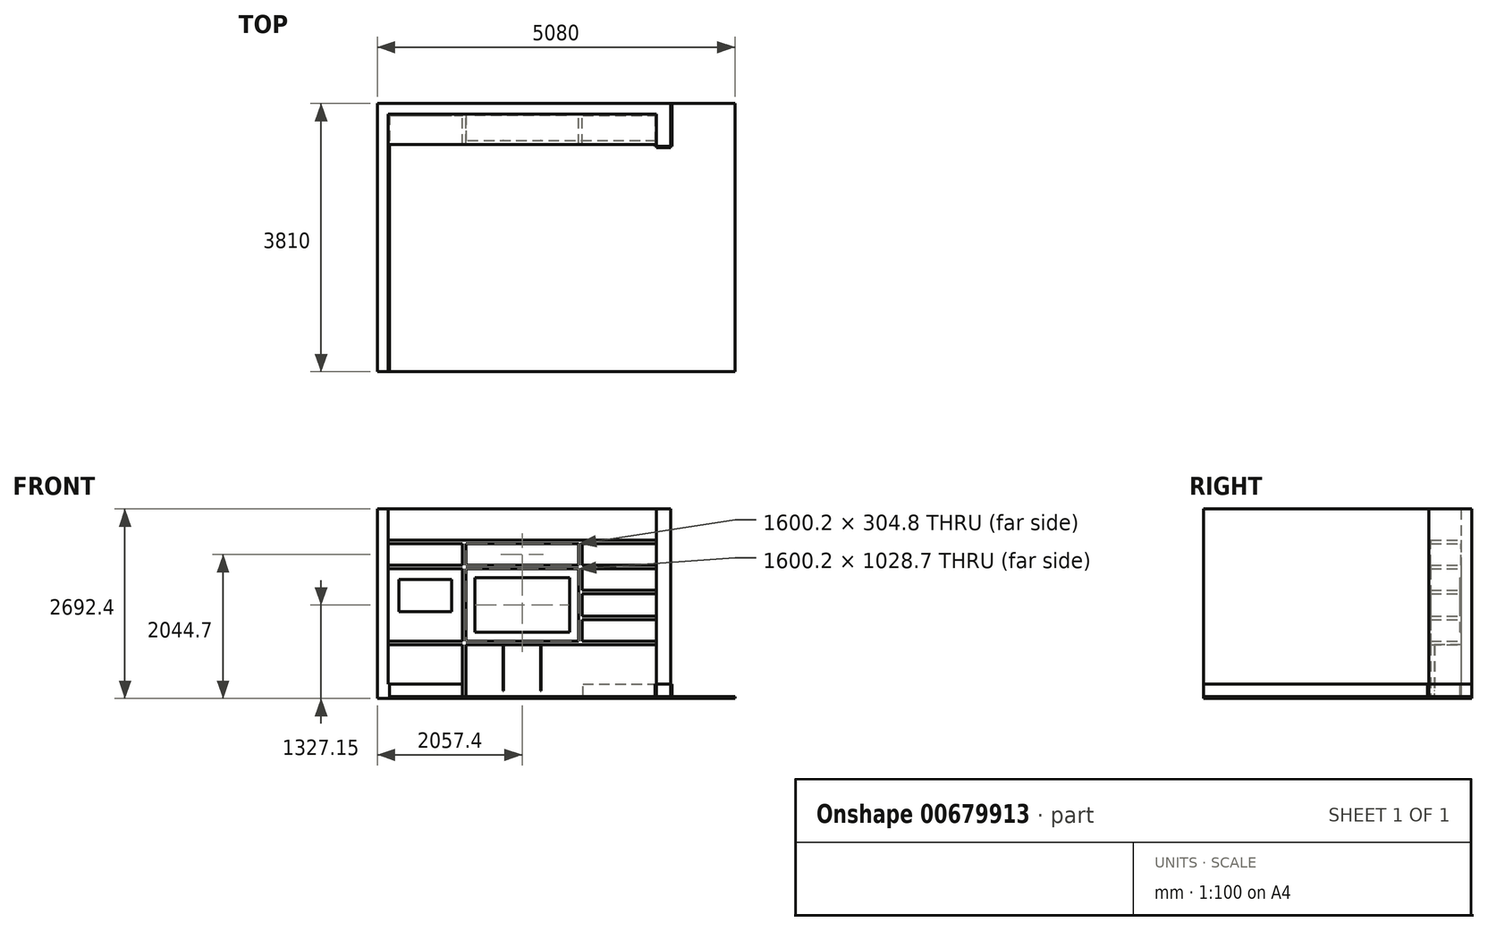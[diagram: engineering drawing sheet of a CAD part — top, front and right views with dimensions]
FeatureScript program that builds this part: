
annotation { "Feature Type Name" : "Feature", "Feature Type Description" : "" }
export const myFeature = defineFeature(function(context is Context, id is Id, definition is map)
    precondition{}
    {
        {
            var Q0;
            Q0=qCreatedBy(makeId("Top.planeOp"),FACE);
            var sketch = newSketch(context, id + "F0", { "sketchPlane" : qUnion([Q0])});
            skLineSegment(sketch, "E0.bottom", {"start": v(2540, 1905) * mm, "end": v(-2540, 1905) * mm});
            skLineSegment(sketch, "E0.top", {"start": v(2540, -1905) * mm, "end": v(-2540, -1905) * mm});
            skLineSegment(sketch, "E0.left", {"start": v(2540, 1905) * mm, "end": v(2540, -1905) * mm});
            skLineSegment(sketch, "E0.right", {"start": v(-2540, 1905) * mm, "end": v(-2540, -1905) * mm});
            skPoint(sketch, "E0.middle", {"position": v(0, 0) * mm});
            skSolve(sketch);
        }
        {
            var Q0;
            Q0=makeQuery(id+"F0.imprint","IMPRINT",FACE,{"disambiguationData":[TD([[makeQuery(id+"F0.imprint","IMPRINT",EDGE,{"derivedFrom":sQuery(id+"F0.wireOp",EDGE,"E0.bottom")}),1.0]])]});
            extrude(context, id + "F1", {"entities" : qUnion([Q0]), "depth" : 25.4 * mm, "offsetDistance" : 25.4 * mm});
        }
        {
            var Q0;
            Q0=makeQuery(id+"F1.opExtrude","CAP_FACE",FACE,{"disambiguationData":[OSD([sQuery(id+"F0.wireOp",EDGE,"E0.bottom"),sQuery(id+"F0.wireOp",EDGE,"E0.top"),sQuery(id+"F0.wireOp",EDGE,"E0.left"),sQuery(id+"F0.wireOp",EDGE,"E0.right")])],"isStart":false});
            var sketch = newSketch(context, id + "F2", { "sketchPlane" : qUnion([Q0])});
            skLineSegment(sketch, "E1", {"start": v(-2387.6, 1905) * mm, "end": v(-2387.6, -1905) * mm, "construction": true});
            skLineSegment(sketch, "E2", {"start": v(-2540, 1752.6) * mm, "end": v(2540, 1752.6) * mm, "construction": true});
            skLineSegment(sketch, "E3", {"start": v(1422.4, 1905) * mm, "end": v(1422.4, 1295.4) * mm, "construction": true});
            skLineSegment(sketch, "E4", {"start": v(1625.6, 1905) * mm, "end": v(1625.6, 1295.4) * mm, "construction": true});
            skLineSegment(sketch, "E5", {"start": v(1422.4, 1295.4) * mm, "end": v(1625.6, 1295.4) * mm, "construction": true});
            skLineSegment(sketch, "E6", {"start": v(-2387.6, -1905) * mm, "end": v(-2387.6, 1752.6) * mm});
            skLineSegment(sketch, "E7", {"start": v(-2387.6, 1752.6) * mm, "end": v(1422.4, 1752.6) * mm});
            skLineSegment(sketch, "E8", {"start": v(1422.4, 1752.6) * mm, "end": v(1422.4, 1295.4) * mm});
            skLineSegment(sketch, "E9", {"start": v(1422.4, 1295.4) * mm, "end": v(1625.6, 1295.4) * mm});
            skLineSegment(sketch, "E10", {"start": v(1625.6, 1295.4) * mm, "end": v(1625.6, 1905) * mm});
            skSolve(sketch);
        }
        {
            var Q0;
            {var subQ0=sQuery(id+"F2.wireOp",EDGE,"E6");Q0=makeQuery(id+"F2.imprint","IMPRINT",FACE,{"disambiguationData":[TD([[makeQuery(id+"F2.imprint","IMPRINT",EDGE,{"derivedFrom":subQ0}),1.0]])]});}
            extrude(context, id + "F3", {"entities" : qUnion([Q0]), "depth" : 2667 * mm, "offsetDistance" : 25.4 * mm});
        }
        {
            var Q0;
            Q0=makeQuery(id+"F3.opExtrude","SWEPT_FACE",FACE,{"disambiguationData":[OSD([sQuery(id+"F2.wireOp",EDGE,"E6")])]});
            var sketch = newSketch(context, id + "F4", { "sketchPlane" : qUnion([Q0])});
            skLineSegment(sketch, "E11.bottom", {"start": v(1752.6, 25.4) * mm, "end": v(-1905, 25.4) * mm});
            skLineSegment(sketch, "E11.top", {"start": v(1752.6, 203.2) * mm, "end": v(-1905, 203.2) * mm});
            skLineSegment(sketch, "E11.left", {"start": v(1752.6, 25.4) * mm, "end": v(1752.6, 203.2) * mm});
            skLineSegment(sketch, "E11.right", {"start": v(-1905, 25.4) * mm, "end": v(-1905, 203.2) * mm});
            skSolve(sketch);
        }
        {
            var Q0;
            Q0=makeQuery(id+"F4.imprint","IMPRINT",FACE,{"disambiguationData":[TD([[makeQuery(id+"F4.imprint","IMPRINT",EDGE,{"derivedFrom":sQuery(id+"F4.wireOp",EDGE,"E11.bottom")}),1.0]])]});
            extrude(context, id + "F5", {"entities" : qUnion([Q0]), "operationType" : NewBodyOperationType.ADD, "depth" : 19.05 * mm, "offsetDistance" : 25.4 * mm});
        }
        {
            var Q0;
            Q0=makeQuery(id+"F3.opExtrude","SWEPT_FACE",FACE,{"disambiguationData":[OSD([sQuery(id+"F2.wireOp",EDGE,"E7")])]});
            var sketch = newSketch(context, id + "F6", { "sketchPlane" : qUnion([Q0])});
            skLineSegment(sketch, "E12.bottom", {"start": v(1422.4, 25.4) * mm, "end": v(-2368.55, 25.4) * mm});
            skLineSegment(sketch, "E12.top", {"start": v(1422.4, 203.2) * mm, "end": v(-2368.55, 203.2) * mm});
            skLineSegment(sketch, "E12.left", {"start": v(1422.4, 25.4) * mm, "end": v(1422.4, 203.2) * mm});
            skLineSegment(sketch, "E12.right", {"start": v(-2368.55, 25.4) * mm, "end": v(-2368.55, 203.2) * mm});
            skSolve(sketch);
        }
        {
            var Q0;
            Q0=makeQuery(id+"F3.opExtrude","SWEPT_FACE",FACE,{"disambiguationData":[OSD([sQuery(id+"F2.wireOp",EDGE,"E8")])]});
            var sketch = newSketch(context, id + "F7", { "sketchPlane" : qUnion([Q0])});
            skLineSegment(sketch, "E13.bottom", {"start": v(-1733.55, 25.4) * mm, "end": v(-1295.4, 25.4) * mm});
            skLineSegment(sketch, "E13.top", {"start": v(-1733.55, 203.2) * mm, "end": v(-1295.4, 203.2) * mm});
            skLineSegment(sketch, "E13.left", {"start": v(-1733.55, 25.4) * mm, "end": v(-1733.55, 203.2) * mm});
            skLineSegment(sketch, "E13.right", {"start": v(-1295.4, 25.4) * mm, "end": v(-1295.4, 203.2) * mm});
            skSolve(sketch);
        }
        {
            var Q0;
            Q0=makeQuery(id+"F7.imprint","IMPRINT",FACE,{"disambiguationData":[TD([[makeQuery(id+"F7.imprint","IMPRINT",EDGE,{"derivedFrom":sQuery(id+"F7.wireOp",EDGE,"E13.bottom")}),1.0]])]});
            extrude(context, id + "F8", {"entities" : qUnion([Q0]), "depth" : 19.05 * mm, "offsetDistance" : 25.4 * mm});
        }
        {
            var Q0;
            Q0=makeQuery(id+"F8.boolean.opBoolean","MERGE",FACE,{"derivedFrom":[makeQuery(id+"F3.opExtrude","SWEPT_FACE",FACE,{"disambiguationData":[OSD([sQuery(id+"F2.wireOp",EDGE,"E9")])]}),makeQuery(id+"F8.opExtrude","SWEPT_FACE",FACE,{"disambiguationData":[OSD([sQuery(id+"F7.wireOp",EDGE,"E13.right")])]})]});
            var sketch = newSketch(context, id + "F9", { "sketchPlane" : qUnion([Q0])});
            skLineSegment(sketch, "E14.bottom", {"start": v(1625.6, 25.4) * mm, "end": v(1403.35, 25.4) * mm});
            skLineSegment(sketch, "E14.top", {"start": v(1625.6, 203.2) * mm, "end": v(1403.35, 203.2) * mm});
            skLineSegment(sketch, "E14.left", {"start": v(1625.6, 25.4) * mm, "end": v(1625.6, 203.2) * mm});
            skLineSegment(sketch, "E14.right", {"start": v(1403.35, 25.4) * mm, "end": v(1403.35, 203.2) * mm});
            skSolve(sketch);
        }
        {
            var Q0;
            Q0=makeQuery(id+"F9.imprint","IMPRINT",FACE,{"disambiguationData":[TD([[makeQuery(id+"F9.imprint","IMPRINT",EDGE,{"derivedFrom":sQuery(id+"F9.wireOp",EDGE,"E14.bottom")}),1.0]])]});
            extrude(context, id + "F10", {"entities" : qUnion([Q0]), "depth" : 19.05 * mm, "offsetDistance" : 25.4 * mm});
        }
        {
            var Q0;
            Q0=makeQuery(id+"F10.boolean.opBoolean","MERGE",FACE,{"derivedFrom":[makeQuery(id+"F3.opExtrude","SWEPT_FACE",FACE,{"disambiguationData":[OSD([sQuery(id+"F2.wireOp",EDGE,"E10")])]}),makeQuery(id+"F10.opExtrude","SWEPT_FACE",FACE,{"disambiguationData":[OSD([sQuery(id+"F9.wireOp",EDGE,"E14.left")])]})]});
            var sketch = newSketch(context, id + "F11", { "sketchPlane" : qUnion([Q0])});
            skLineSegment(sketch, "E15.bottom", {"start": v(1905, 25.4) * mm, "end": v(1276.35, 25.4) * mm});
            skLineSegment(sketch, "E15.top", {"start": v(1905, 203.2) * mm, "end": v(1276.35, 203.2) * mm});
            skLineSegment(sketch, "E15.left", {"start": v(1905, 25.4) * mm, "end": v(1905, 203.2) * mm});
            skLineSegment(sketch, "E15.right", {"start": v(1276.35, 25.4) * mm, "end": v(1276.35, 203.2) * mm});
            skSolve(sketch);
        }
        {
            var Q0;
            Q0=makeQuery(id+"F11.imprint","IMPRINT",FACE,{"disambiguationData":[TD([[makeQuery(id+"F11.imprint","IMPRINT",EDGE,{"derivedFrom":sQuery(id+"F11.wireOp",EDGE,"E15.bottom")}),1.0]])]});
            extrude(context, id + "F12", {"entities" : qUnion([Q0]), "depth" : 19.05 * mm, "offsetDistance" : 25.4 * mm});
        }
        {
            var Q0;
            Q0=makeQuery(id+"F3.opExtrude","SWEPT_FACE",FACE,{"disambiguationData":[OSD([sQuery(id+"F2.wireOp",EDGE,"E7")])]});
            var sketch = newSketch(context, id + "F13", { "sketchPlane" : qUnion([Q0])});
            skLineSegment(sketch, "E16", {"start": v(-2387.6, 939.8) * mm, "end": v(1422.4, 939.8) * mm, "construction": true});
            skLineSegment(sketch, "E17", {"start": v(-2387.6, 1714.5) * mm, "end": v(1422.4, 1714.5) * mm, "construction": true});
            skLineSegment(sketch, "E18", {"start": v(-482.6, 25.4) * mm, "end": v(-482.6, 2692.4) * mm, "construction": true});
            skLineSegment(sketch, "E19", {"start": v(-1155.7, 1714.5) * mm, "end": v(-1155.7, 939.8) * mm, "construction": true});
            skLineSegment(sketch, "E20", {"start": v(190.5, 1714.5) * mm, "end": v(190.5, 939.8) * mm, "construction": true});
            skLineSegment(sketch, "E21", {"start": v(-1155.7, 1714.5) * mm, "end": v(190.5, 1714.5) * mm});
            skLineSegment(sketch, "E22", {"start": v(190.5, 1714.5) * mm, "end": v(190.5, 939.8) * mm});
            skLineSegment(sketch, "E23", {"start": v(190.5, 939.8) * mm, "end": v(-1155.7, 939.8) * mm});
            skLineSegment(sketch, "E24", {"start": v(-1155.7, 939.8) * mm, "end": v(-1155.7, 1714.5) * mm});
            skSolve(sketch);
        }
        {
            var Q0;
            Q0=makeQuery(id+"F13.imprint","IMPRINT",FACE,{"disambiguationData":[TD([[makeQuery(id+"F13.imprint","IMPRINT",EDGE,{"derivedFrom":sQuery(id+"F13.wireOp",EDGE,"E21")}),-1.0]])]});
            extrude(context, id + "F14", {"entities" : qUnion([Q0]), "depth" : 12.7 * mm, "offsetDistance" : 25.4 * mm});
        }
        {
            var Q0;
            Q0=makeQuery(id+"F3.opExtrude","SWEPT_FACE",FACE,{"disambiguationData":[OSD([sQuery(id+"F2.wireOp",EDGE,"E7")])]});
            var sketch = newSketch(context, id + "F15", { "sketchPlane" : qUnion([Q0])});
            skLineSegment(sketch, "E25", {"start": v(1422.4, 787.4) * mm, "end": v(-2387.6, 787.4) * mm, "construction": true});
            skLineSegment(sketch, "E26", {"start": v(-2387.6, 1866.9) * mm, "end": v(1422.4, 1866.9) * mm, "construction": true});
            skLineSegment(sketch, "E27", {"start": v(-2387.6, 2222.5) * mm, "end": v(1422.4, 2222.5) * mm, "construction": true});
            skLineSegment(sketch, "E28", {"start": v(342.9, 1866.9) * mm, "end": v(342.9, 25.4) * mm, "construction": true});
            skLineSegment(sketch, "E29", {"start": v(-1308.1, 1866.9) * mm, "end": v(-1308.1, 25.4) * mm, "construction": true});
            skLineSegment(sketch, "E30", {"start": v(-2387.6, 1892.3) * mm, "end": v(1422.4, 1892.3) * mm});
            skLineSegment(sketch, "E31", {"start": v(-2387.6, 1841.5) * mm, "end": v(1422.4, 1841.5) * mm});
            skLineSegment(sketch, "E32", {"start": v(-2387.6, 2247.9) * mm, "end": v(1422.4, 2247.9) * mm});
            skLineSegment(sketch, "E33", {"start": v(-2387.6, 2197.1) * mm, "end": v(1422.4, 2197.1) * mm});
            skLineSegment(sketch, "E34", {"start": v(-1333.5, 1841.5) * mm, "end": v(-1333.5, 25.4) * mm});
            skLineSegment(sketch, "E35", {"start": v(-1282.7, 1841.5) * mm, "end": v(-1282.7, 25.4) * mm});
            skLineSegment(sketch, "E36", {"start": v(368.3, 1841.5) * mm, "end": v(368.3, 25.4) * mm});
            skLineSegment(sketch, "E37", {"start": v(317.5, 1841.5) * mm, "end": v(317.5, 25.4) * mm});
            skLineSegment(sketch, "E38", {"start": v(-2387.6, 812.8) * mm, "end": v(1422.4, 812.8) * mm});
            skLineSegment(sketch, "E39", {"start": v(-2387.6, 762) * mm, "end": v(1422.4, 762) * mm});
            skLineSegment(sketch, "E40", {"start": v(-1333.5, 1841.5) * mm, "end": v(-1333.5, 2222.5) * mm});
            skLineSegment(sketch, "E41", {"start": v(-1282.7, 1841.5) * mm, "end": v(-1282.7, 2247.9) * mm});
            skLineSegment(sketch, "E42", {"start": v(317.5, 1841.5) * mm, "end": v(317.5, 2197.1) * mm});
            skLineSegment(sketch, "E43", {"start": v(368.3, 1841.5) * mm, "end": v(368.3, 2197.1) * mm});
            skLineSegment(sketch, "E44", {"start": v(368.3, 1143) * mm, "end": v(1422.4, 1143) * mm, "construction": true});
            skLineSegment(sketch, "E45", {"start": v(368.3, 1511.3) * mm, "end": v(1422.4, 1511.3) * mm, "construction": true});
            skLineSegment(sketch, "E46", {"start": v(368.3, 1536.7) * mm, "end": v(1422.4, 1536.7) * mm});
            skLineSegment(sketch, "E47", {"start": v(368.3, 1485.9) * mm, "end": v(1422.4, 1485.9) * mm});
            skLineSegment(sketch, "E48", {"start": v(368.3, 1168.4) * mm, "end": v(1422.4, 1168.4) * mm});
            skLineSegment(sketch, "E49", {"start": v(368.3, 1117.6) * mm, "end": v(1422.4, 1117.6) * mm});
            skSolve(sketch);
        }
        {
            var Q0;
            {var subQ0=sQuery(id+"F15.wireOp",EDGE,"E32");Q0=makeQuery(id+"F15.imprint","IMPRINT",FACE,{"disambiguationData":[TD([[makeQuery(id+"F15.imprint","IMPRINT",EDGE,{"derivedFrom":subQ0}),-1.0]])]});}
            var Q1;
            {var subQ7=sQuery(id+"F15.wireOp",EDGE,"E30");Q1=makeQuery(id+"F15.imprint","IMPRINT",FACE,{"disambiguationData":[TD([[makeQuery(id+"F15.imprint","IMPRINT",EDGE,{"derivedFrom":subQ7}),-1.0]])]});}
            var Q2;
            {var subQ0=sQuery(id+"F15.wireOp",EDGE,"E34");var subQ1=sQuery(id+"F15.wireOp",EDGE,"E31");var subQ2=makeQuery(id+"F15.imprint","INTERSECT",VERTEX,{"derivedFrom":[subQ1,subQ0]});Q2=makeQuery(id+"F15.imprint","IMPRINT",FACE,{"disambiguationData":[TD([[makeQuery(id+"F15.imprint","IMPRINT",EDGE,{"disambiguationData":[TD([[subQ2,-1.0]])],"derivedFrom":subQ1}),-1.0]])]});}
            var Q3;
            {var subQ0=sQuery(id+"F15.wireOp",EDGE,"E36");var subQ5=sQuery(id+"F15.wireOp",EDGE,"E31");var subQ6=makeQuery(id+"F15.imprint","INTERSECT",VERTEX,{"derivedFrom":[subQ5,subQ0]});Q3=makeQuery(id+"F15.imprint","IMPRINT",FACE,{"disambiguationData":[TD([[makeQuery(id+"F15.imprint","IMPRINT",EDGE,{"disambiguationData":[TD([[subQ6,1.0]])],"derivedFrom":subQ5}),-1.0]])]});}
            var Q4;
            {var subQ0=sQuery(id+"F15.wireOp",EDGE,"W6vbu9uU-liGj-dEqg-lg2W-kPpZRO7yYNNE");Q4=makeQuery(id+"F15.imprint","IMPRINT",FACE,{"disambiguationData":[TD([[makeQuery(id+"F15.imprint","IMPRINT",EDGE,{"derivedFrom":subQ0}),-1.0]])]});}
            var Q5;
            {var subQ0=sQuery(id+"F15.wireOp",EDGE,"E38");var subQ1=sQuery(id+"F15.wireOp",EDGE,"E36");var subQ2=makeQuery(id+"F15.imprint","INTERSECT",VERTEX,{"derivedFrom":[subQ1,subQ0]});Q5=makeQuery(id+"F15.imprint","IMPRINT",FACE,{"disambiguationData":[TD([[makeQuery(id+"F15.imprint","IMPRINT",EDGE,{"disambiguationData":[TD([[subQ2,-1.0]])],"derivedFrom":subQ1}),1.0]])]});}
            var Q6;
            {var subQ0=sQuery(id+"F15.wireOp",EDGE,"E38");var subQ1=sQuery(id+"F15.wireOp",EDGE,"E36");var subQ2=makeQuery(id+"F15.imprint","INTERSECT",VERTEX,{"derivedFrom":[subQ1,subQ0]});Q6=makeQuery(id+"F15.imprint","IMPRINT",FACE,{"disambiguationData":[TD([[makeQuery(id+"F15.imprint","IMPRINT",EDGE,{"disambiguationData":[TD([[subQ2,-1.0]])],"derivedFrom":subQ1}),-1.0]])]});}
            var Q7;
            {var subQ0=sQuery(id+"F15.wireOp",EDGE,"E38");var subQ1=sQuery(id+"F15.wireOp",EDGE,"E35");var subQ2=makeQuery(id+"F15.imprint","INTERSECT",VERTEX,{"derivedFrom":[subQ1,subQ0]});Q7=makeQuery(id+"F15.imprint","IMPRINT",FACE,{"disambiguationData":[TD([[makeQuery(id+"F15.imprint","IMPRINT",EDGE,{"disambiguationData":[TD([[subQ2,-1.0]])],"derivedFrom":subQ1}),1.0]])]});}
            var Q8;
            {var subQ0=sQuery(id+"F15.wireOp",EDGE,"E36");var subQ1=makeQuery(id+"F3.opExtrude","CAP_EDGE",EDGE,{"disambiguationData":[OSD([sQuery(id+"F2.wireOp",EDGE,"E7")])],"isStart":true});var subQ2=makeQuery(id+"F15.imprint","INTERSECT",VERTEX,{"derivedFrom":[subQ1,subQ0]});Q8=makeQuery(id+"F15.imprint","IMPRINT",FACE,{"disambiguationData":[TD([[makeQuery(id+"F15.imprint","IMPRINT",EDGE,{"disambiguationData":[TD([[subQ2,1.0]])],"derivedFrom":subQ0}),-1.0]])]});}
            var Q9;
            {var subQ0=sQuery(id+"F15.wireOp",EDGE,"E38");var subQ1=sQuery(id+"F15.wireOp",EDGE,"E34");var subQ2=makeQuery(id+"F15.imprint","INTERSECT",VERTEX,{"derivedFrom":[subQ1,subQ0]});Q9=makeQuery(id+"F15.imprint","IMPRINT",FACE,{"disambiguationData":[TD([[makeQuery(id+"F15.imprint","IMPRINT",EDGE,{"disambiguationData":[TD([[subQ2,-1.0]])],"derivedFrom":subQ1}),1.0]])]});}
            var Q10;
            {var subQ0=sQuery(id+"F15.wireOp",EDGE,"E34");var subQ1=makeQuery(id+"F3.opExtrude","CAP_EDGE",EDGE,{"disambiguationData":[OSD([sQuery(id+"F2.wireOp",EDGE,"E7")])],"isStart":true});var subQ2=makeQuery(id+"F15.imprint","INTERSECT",VERTEX,{"derivedFrom":[subQ1,subQ0]});Q10=makeQuery(id+"F15.imprint","IMPRINT",FACE,{"disambiguationData":[TD([[makeQuery(id+"F15.imprint","IMPRINT",EDGE,{"disambiguationData":[TD([[subQ2,1.0]])],"derivedFrom":subQ0}),1.0]])]});}
            var Q11;
            {var subQ0=sQuery(id+"F15.wireOp",EDGE,"E38");var subQ1=sQuery(id+"F15.wireOp",EDGE,"E34");var subQ2=makeQuery(id+"F15.imprint","INTERSECT",VERTEX,{"derivedFrom":[subQ1,subQ0]});Q11=makeQuery(id+"F15.imprint","IMPRINT",FACE,{"disambiguationData":[TD([[makeQuery(id+"F15.imprint","IMPRINT",EDGE,{"disambiguationData":[TD([[subQ2,-1.0]])],"derivedFrom":subQ1}),-1.0]])]});}
            var Q12;
            {var subQ0=sQuery(id+"F15.wireOp",EDGE,"E48");Q12=makeQuery(id+"F15.imprint","IMPRINT",FACE,{"disambiguationData":[TD([[makeQuery(id+"F15.imprint","IMPRINT",EDGE,{"derivedFrom":subQ0}),-1.0]])]});}
            var Q13;
            {var subQ0=sQuery(id+"F15.wireOp",EDGE,"E46");Q13=makeQuery(id+"F15.imprint","IMPRINT",FACE,{"disambiguationData":[TD([[makeQuery(id+"F15.imprint","IMPRINT",EDGE,{"derivedFrom":subQ0}),-1.0]])]});}
            var Q14;
            {var subQ0=sQuery(id+"F15.wireOp",EDGE,"E42");var subQ1=sQuery(id+"F15.wireOp",EDGE,"E30");var subQ2=makeQuery(id+"F15.imprint","INTERSECT",VERTEX,{"derivedFrom":[subQ1,subQ0]});Q14=makeQuery(id+"F15.imprint","IMPRINT",FACE,{"disambiguationData":[TD([[makeQuery(id+"F15.imprint","IMPRINT",EDGE,{"disambiguationData":[TD([[subQ2,-1.0]])],"derivedFrom":subQ1}),1.0]])]});}
            var Q15;
            {var subQ0=sQuery(id+"F15.wireOp",EDGE,"E40");var subQ1=sQuery(id+"F15.wireOp",EDGE,"E30");var subQ2=makeQuery(id+"F15.imprint","INTERSECT",VERTEX,{"derivedFrom":[subQ1,subQ0]});Q15=makeQuery(id+"F15.imprint","IMPRINT",FACE,{"disambiguationData":[TD([[makeQuery(id+"F15.imprint","IMPRINT",EDGE,{"disambiguationData":[TD([[subQ2,-1.0]])],"derivedFrom":subQ1}),1.0]])]});}
            var Q16;
            {var subQ0=sQuery(id+"F15.wireOp",EDGE,"E33");var subQ1=makeQuery(id+"F15.imprint","INTERSECT",VERTEX,{"derivedFrom":[subQ0,sQuery(id+"F15.wireOp",EDGE,"E42")]});Q16=makeQuery(id+"F15.imprint","IMPRINT",FACE,{"disambiguationData":[TD([[makeQuery(id+"F15.imprint","IMPRINT",EDGE,{"disambiguationData":[TD([[subQ1,1.0]])],"derivedFrom":subQ0}),1.0]])]});}
            extrude(context, id + "F16", {"entities" : qUnion([Q0, Q1, Q2, Q3, Q4, Q5, Q6, Q7, Q8, Q9, Q10, Q11, Q12, Q13, Q14, Q15, Q16]), "depth" : 431.8 * mm, "offsetDistance" : 25.4 * mm});
        }
        {
            var Q0;
            {var subQ0=sQuery(id+"F15.wireOp",EDGE,"E35");Q0=makeQuery(id+"F16.opExtrude","SWEPT_FACE",FACE,{"disambiguationData":[OSD([subQ0]),TDD([makeQuery(id+"F15.imprint","IMPRINT",EDGE,{"disambiguationData":[TD([[makeQuery(id+"F15.imprint","INTERSECT",VERTEX,{"derivedFrom":[makeQuery(id+"F3.opExtrude","CAP_EDGE",EDGE,{"disambiguationData":[OSD([sQuery(id+"F2.wireOp",EDGE,"E7")])],"isStart":true}),subQ0]}),1.0]])],"derivedFrom":subQ0})])]});}
            var sketch = newSketch(context, id + "F17", { "sketchPlane" : qUnion([Q0])});
            skLineSegment(sketch, "E50.bottom", {"start": v(1752.6, 762) * mm, "end": v(1371.6, 762) * mm});
            skLineSegment(sketch, "E50.top", {"start": v(1752.6, 25.4) * mm, "end": v(1371.6, 25.4) * mm});
            skLineSegment(sketch, "E50.left", {"start": v(1752.6, 762) * mm, "end": v(1752.6, 25.4) * mm});
            skLineSegment(sketch, "E50.right", {"start": v(1371.6, 762) * mm, "end": v(1371.6, 25.4) * mm});
            skSolve(sketch);
        }
        {
            var Q0;
            Q0 = qSketchRegion(id + "F17", true);
            extrude(context, id + "F18", {"entities" : qUnion([Q0]), "endBound" : BoundingType.UP_TO_NEXT, "depth" : 25.4 * mm, "offsetDistance" : 25.4 * mm});
        }
        {
            var Q0;
            Q0=makeQuery(id+"F18.opExtrude","SWEPT_FACE",FACE,{"disambiguationData":[OSD([sQuery(id+"F17.wireOp",EDGE,"E50.right")])]});
            var sketch = newSketch(context, id + "F19", { "sketchPlane" : qUnion([Q0])});
            skLineSegment(sketch, "E51", {"start": v(-1282.7, 101.6) * mm, "end": v(317.5, 101.6) * mm});
            skLineSegment(sketch, "E52", {"start": v(-1282.7, 107.95) * mm, "end": v(317.5, 107.95) * mm});
            skLineSegment(sketch, "E53", {"start": v(-749.3, 762) * mm, "end": v(-749.3, 107.95) * mm, "construction": true});
            skLineSegment(sketch, "E54", {"start": v(-215.9, 762) * mm, "end": v(-215.9, 107.95) * mm, "construction": true});
            skLineSegment(sketch, "E55", {"start": v(-752.47, 762) * mm, "end": v(-752.47, 107.95) * mm});
            skLineSegment(sketch, "E56", {"start": v(-746.12, 762) * mm, "end": v(-746.12, 107.95) * mm});
            skLineSegment(sketch, "E57", {"start": v(-219.07, 762) * mm, "end": v(-219.07, 107.95) * mm});
            skLineSegment(sketch, "E58", {"start": v(-212.72, 762) * mm, "end": v(-212.72, 107.95) * mm});
            skSolve(sketch);
        }
        {
            var Q0;
            Q0=makeQuery(id+"F3.opExtrude","SWEPT_FACE",FACE,{"disambiguationData":[OSD([sQuery(id+"F2.wireOp",EDGE,"E7")])]});
            var sketch = newSketch(context, id + "F20", { "sketchPlane" : qUnion([Q0])});
            skLineSegment(sketch, "E59", {"start": v(-1485.9, 1689.1) * mm, "end": v(-1485.9, 829.43) * mm, "construction": true});
            skLineSegment(sketch, "E60", {"start": v(-2235.2, 1697.78) * mm, "end": v(-2235.2, 890.22) * mm, "construction": true});
            skLineSegment(sketch, "E61", {"start": v(-2235.2, 1231.9) * mm, "end": v(-1485.9, 1231.9) * mm, "construction": true});
            skLineSegment(sketch, "E62", {"start": v(-1485.9, 1689.1) * mm, "end": v(-2235.2, 1689.1) * mm, "construction": true});
            skLineSegment(sketch, "E63", {"start": v(-2235.2, 1697.78) * mm, "end": v(-2235.2, 1231.9) * mm});
            skLineSegment(sketch, "E64", {"start": v(-2235.2, 1231.9) * mm, "end": v(-1485.9, 1231.9) * mm});
            skLineSegment(sketch, "E65", {"start": v(-1485.9, 1231.9) * mm, "end": v(-1485.9, 1689.1) * mm});
            skLineSegment(sketch, "E66", {"start": v(-2235.2, 1689.1) * mm, "end": v(-1485.9, 1689.1) * mm});
            skSolve(sketch);
        }
        {
            var Q0;
            Q0 = qSketchRegion(id + "F20", true);
            extrude(context, id + "F21", {"entities" : qUnion([Q0]), "depth" : 19.05 * mm, "offsetDistance" : 25.4 * mm});
        }
        {
            var Q0;
            Q0 = qSketchRegion(id + "F20", true);
            extrude(context, id + "F22", {"entities" : qUnion([Q0]), "depth" : 19.05 * mm, "offsetDistance" : 25.4 * mm});
        }
        {
            var Q0;
            Q0=makeQuery(id+"F3.opExtrude","SWEPT_EDGE",EDGE,{"disambiguationData":[OSD([sQuery(id+"F2.wireOp",EDGE,"E8"),sQuery(id+"F2.wireOp",EDGE,"E9")])]});
            var Q1;
            Q1=makeQuery(id+"F3.opExtrude","SWEPT_EDGE",EDGE,{"disambiguationData":[OSD([sQuery(id+"F2.wireOp",EDGE,"E9"),sQuery(id+"F2.wireOp",EDGE,"E10")])]});
            var Q2;
            Q2=makeQuery(id+"F10.opExtrude","CAP_EDGE",EDGE,{"disambiguationData":[OSD([sQuery(id+"F9.wireOp",EDGE,"E14.right")])],"isStart":false});
            var Q3;
            Q3=makeQuery(id+"F12.opExtrude","CAP_EDGE",EDGE,{"disambiguationData":[OSD([sQuery(id+"F11.wireOp",EDGE,"E15.right")])],"isStart":false});
            fillet(context, id + "F23", {"entities" : qUnion([Q0, Q1, Q2, Q3]), "radius" : 12.7 * mm, "tangentPropagation" : true, "allowEdgeOverflow" : false});
        }
        {
            var Q0;
            Q0=makeQuery(id+"F3.opExtrude","SWEPT_FACE",FACE,{"disambiguationData":[OSD([sQuery(id+"F2.wireOp",EDGE,"E7")])]});
            var sketch = newSketch(context, id + "F24", { "sketchPlane" : qUnion([Q0])});
            skLineSegment(sketch, "E67.bottom", {"start": v(379.2, 25.4) * mm, "end": v(1422.4, 25.4) * mm});
            skLineSegment(sketch, "E67.top", {"start": v(379.2, 203.2) * mm, "end": v(1422.4, 203.2) * mm});
            skLineSegment(sketch, "E67.left", {"start": v(379.2, 25.4) * mm, "end": v(379.2, 203.2) * mm});
            skLineSegment(sketch, "E67.right", {"start": v(1422.4, 25.4) * mm, "end": v(1422.4, 203.2) * mm});
            skSolve(sketch);
        }
        {
            var Q0;
            Q0 = qSketchRegion(id + "F24", true);
            extrude(context, id + "F25", {"entities" : qUnion([Q0]), "depth" : 19.05 * mm, "offsetDistance" : 25.4 * mm});
        }
        {
            var Q0;
            Q0=makeQuery(id+"F3.opExtrude","SWEPT_FACE",FACE,{"disambiguationData":[OSD([sQuery(id+"F2.wireOp",EDGE,"E7")])]});
            var sketch = newSketch(context, id + "F26", { "sketchPlane" : qUnion([Q0])});
            skLineSegment(sketch, "E68.bottom", {"start": v(-2368.55, 203.2) * mm, "end": v(-1324.86, 203.2) * mm});
            skLineSegment(sketch, "E68.top", {"start": v(-2368.55, 25.4) * mm, "end": v(-1324.86, 25.4) * mm});
            skLineSegment(sketch, "E68.left", {"start": v(-2368.55, 203.2) * mm, "end": v(-2368.55, 25.4) * mm});
            skLineSegment(sketch, "E68.right", {"start": v(-1324.86, 203.2) * mm, "end": v(-1324.86, 25.4) * mm});
            skSolve(sketch);
        }
        {
            var Q0;
            Q0 = qSketchRegion(id + "F26", true);
            extrude(context, id + "F27", {"entities" : qUnion([Q0]), "depth" : 19.05 * mm, "offsetDistance" : 25.4 * mm});
        }
        {
            var Q0;
            {var subQ4=sQuery(id+"F19.wireOp",EDGE,"E51");Q0=makeQuery(id+"F19.imprint","IMPRINT",FACE,{"disambiguationData":[TD([[makeQuery(id+"F19.imprint","IMPRINT",EDGE,{"derivedFrom":subQ4}),1.0]])]});}
            var Q1;
            {var subQ0=sQuery(id+"F19.wireOp",EDGE,"E57");Q1=makeQuery(id+"F19.imprint","IMPRINT",FACE,{"disambiguationData":[TD([[makeQuery(id+"F19.imprint","IMPRINT",EDGE,{"derivedFrom":subQ0}),1.0]])]});}
            var Q2;
            {var subQ0=sQuery(id+"F19.wireOp",EDGE,"E55");Q2=makeQuery(id+"F19.imprint","IMPRINT",FACE,{"disambiguationData":[TD([[makeQuery(id+"F19.imprint","IMPRINT",EDGE,{"derivedFrom":subQ0}),1.0]])]});}
            extrude(context, id + "F28", {"entities" : qUnion([Q0, Q1, Q2]), "oppositeDirection" : true, "depth" : 6.35 * mm, "offsetDistance" : 25.4 * mm});
        }
    });
